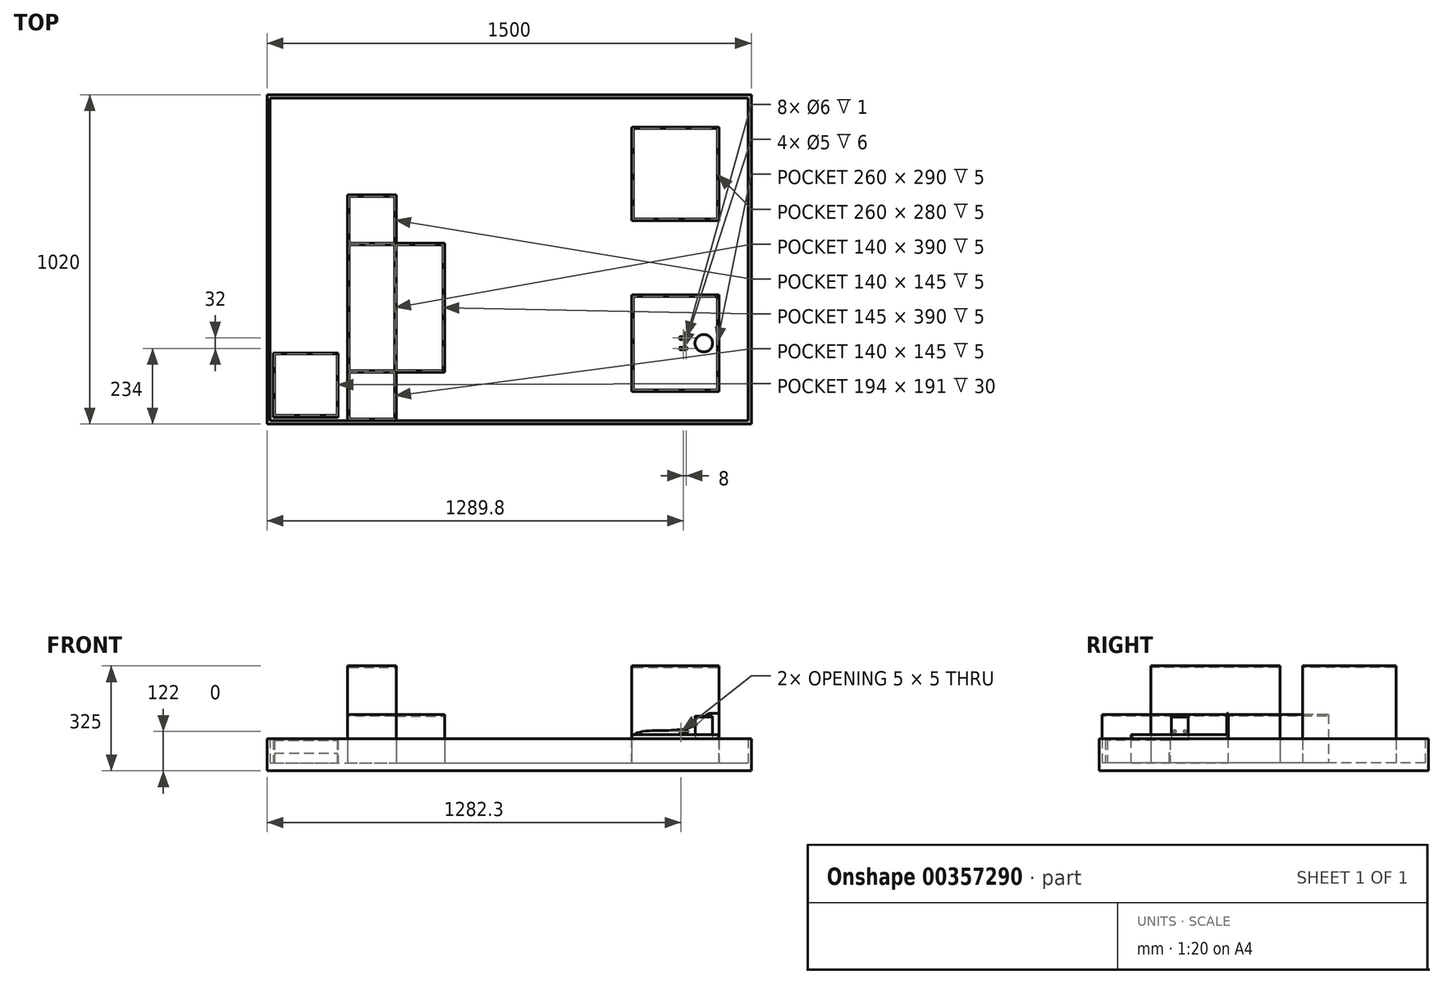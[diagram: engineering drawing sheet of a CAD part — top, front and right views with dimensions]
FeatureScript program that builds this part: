
annotation { "Feature Type Name" : "Feature", "Feature Type Description" : "" }
export const myFeature = defineFeature(function(context is Context, id is Id, definition is map)
    precondition{}
    {
        {
            var Q0;
            Q0=qCreatedBy(makeId("Top.planeOp"),FACE);
            var sketch = newSketch(context, id + "F0", { "sketchPlane" : qUnion([Q0])});
            skCircle(sketch, "E0", {"center": v(0, 0) * mm, "radius": 27.2 * mm});
            skSolve(sketch);
        }
        {
            var Q0;
            Q0=qSketchRegion(id+"F0",true);
            extrude(context, id + "F1", {"entities" : qUnion([Q0]), "depth" : 2.83 * mm});
        }
        {
            var Q0;
            Q0=makeQuery(id+"F1.opExtrude","CAP_FACE",FACE,{"disambiguationData":[OSD([sQuery(id+"F0.wireOp",EDGE,"E0")])],"isStart":false});
            var sketch = newSketch(context, id + "F2", { "sketchPlane" : qUnion([Q0])});
            skCircle(sketch, "E1", {"center": v(0, 0) * mm, "radius": 26.4 * mm});
            skSolve(sketch);
        }
        {
            var Q0;
            Q0=qSketchRegion(id+"F2",true);
            extrude(context, id + "F3", {"entities" : qUnion([Q0]), "operationType" : NewBodyOperationType.ADD, "depth" : 67.36 * mm});
        }
        {
            var Q0;
            Q0=makeQuery(id+"F3.opExtrude","CAP_FACE",FACE,{"disambiguationData":[OSD([sQuery(id+"F2.wireOp",EDGE,"E1")])],"isStart":false});
            var sketch = newSketch(context, id + "F4", { "sketchPlane" : qUnion([Q0])});
            skCircle(sketch, "E2", {"center": v(0, 0) * mm, "radius": 27.2 * mm});
            skSolve(sketch);
        }
        {
            var Q0;
            Q0=qSketchRegion(id+"F4",true);
            extrude(context, id + "F5", {"entities" : qUnion([Q0]), "operationType" : NewBodyOperationType.ADD, "depth" : 2.83 * mm});
        }
        {
            var Q0;
            Q0=makeQuery(id+"F5.opExtrude","CAP_FACE",FACE,{"disambiguationData":[OSD([sQuery(id+"F4.wireOp",EDGE,"E2")])],"isStart":false});
            var sketch = newSketch(context, id + "F6", { "sketchPlane" : qUnion([Q0])});
            skSolve(sketch);
        }
        {
            var Q0;
            Q0=qCreatedBy(makeId("Top.planeOp"),FACE);
            cPlane(context, id + "F7", {"entities" : qUnion([Q0]), "cplaneType" : CPlaneType.OFFSET, "offset" : 25 * mm, "width" : 150 * mm, "height" : 150 * mm});
        }
        {
            var Q0;
            Q0=makeQuery(id+"F6.imprint","IMPRINT",FACE,{"disambiguationData":[TD([[makeQuery(id+"F6.imprint","IMPRINT",EDGE,{"derivedFrom":makeQuery(id+"F5.opExtrude","CAP_EDGE",EDGE,{"disambiguationData":[OSD([sQuery(id+"F4.wireOp",EDGE,"E2")])],"isStart":false})}),1.0]])]});
            var sketch = newSketch(context, id + "F8", { "sketchPlane" : qUnion([Q0])});
            skSolve(sketch);
        }
        {
            var Q0;
            Q0=qCreatedBy(makeId("Top.planeOp"),FACE);
            var sketch = newSketch(context, id + "F9", { "sketchPlane" : qUnion([Q0])});
            skLineSegment(sketch, "E3.bottom", {"start": v(-222.8, -150) * mm, "end": v(47.2, -150) * mm});
            skLineSegment(sketch, "E3.top", {"start": v(-222.8, 150) * mm, "end": v(47.2, 150) * mm});
            skLineSegment(sketch, "E3.left", {"start": v(-222.8, -150) * mm, "end": v(-222.8, 150) * mm});
            skLineSegment(sketch, "E3.right", {"start": v(47.2, -150) * mm, "end": v(47.2, 150) * mm});
            skSolve(sketch);
        }
        {
            var Q0;
            Q0=qSketchRegion(id+"F9",true);
            extrude(context, id + "F10", {"entities" : qUnion([Q0]), "oppositeDirection" : true, "depth" : 72 * mm});
        }
        {
            var Q0;
            Q0=makeQuery(id+"F10.opExtrude","CAP_FACE",FACE,{"disambiguationData":[OSD([sQuery(id+"F9.wireOp",EDGE,"E3.bottom"),sQuery(id+"F9.wireOp",EDGE,"E3.top"),sQuery(id+"F9.wireOp",EDGE,"E3.left"),sQuery(id+"F9.wireOp",EDGE,"E3.right")])],"isStart":true});
            var sketch = newSketch(context, id + "F11", { "sketchPlane" : qUnion([Q0])});
            skLineSegment(sketch, "E4.bottom", {"start": v(-222.8, -150) * mm, "end": v(47.2, -150) * mm});
            skLineSegment(sketch, "E4.top", {"start": v(-222.8, -145) * mm, "end": v(42.2, -145) * mm});
            skLineSegment(sketch, "E4.left", {"start": v(-222.8, -150) * mm, "end": v(-222.8, -145) * mm});
            skLineSegment(sketch, "E5.bottom", {"start": v(47.2, 150) * mm, "end": v(42.2, 150) * mm});
            skLineSegment(sketch, "E5.left", {"start": v(47.2, 150) * mm, "end": v(47.2, -150) * mm});
            skLineSegment(sketch, "E5.right", {"start": v(42.2, 150) * mm, "end": v(42.2, -145) * mm});
            skSolve(sketch);
        }
        {
            var Q0;
            Q0=qSketchRegion(id+"F11",true);
            extrude(context, id + "F12", {"entities" : qUnion([Q0]), "operationType" : NewBodyOperationType.ADD, "depth" : 15 * mm});
        }
        {
            var Q0;
            Q0=makeQuery(id+"F12.boolean.opBoolean","MERGE",FACE,{"derivedFrom":[makeQuery(id+"F10.opExtrude","SWEPT_FACE",FACE,{"disambiguationData":[OSD([sQuery(id+"F9.wireOp",EDGE,"E3.top")])]}),makeQuery(id+"F12.opExtrude","SWEPT_FACE",FACE,{"disambiguationData":[OSD([sQuery(id+"F11.wireOp",EDGE,"E5.bottom")])]})]});
            var sketch = newSketch(context, id + "F13", { "sketchPlane" : qUnion([Q0])});
            skLineSegment(sketch, "E6", {"start": v(-47.2, 81.36) * mm, "end": v(-21.31, 81.36) * mm});
            skFitSpline(sketch, "E7", {"points": [v(-21.31, 81.36) * mm, v(15.24, 52.01) * mm, v(114.14, 28.17) * mm, v(222.8, 0) * mm], "startDerivative": vector(181.02, 0.3) * mm, "endDerivative": vector(-1.73, -239.85) * mm});
            skLineSegment(sketch, "E8", {"start": v(-47.2, 81.36) * mm, "end": v(-47.2, -72) * mm});
            skLineSegment(sketch, "E9", {"start": v(-47.2, -72) * mm, "end": v(222.8, -72) * mm});
            skLineSegment(sketch, "E10", {"start": v(222.8, -72) * mm, "end": v(222.8, 0) * mm});
            skSolve(sketch);
        }
        {
            var Q0;
            Q0=qSketchRegion(id+"F13",true);
            extrude(context, id + "F14", {"entities" : qUnion([Q0]), "operationType" : NewBodyOperationType.ADD, "oppositeDirection" : true, "depth" : 5 * mm});
        }
        {
            var Q0;
            Q0=makeQuery(id+"F10.opExtrude","CAP_FACE",FACE,{"disambiguationData":[OSD([sQuery(id+"F9.wireOp",EDGE,"E3.bottom"),sQuery(id+"F9.wireOp",EDGE,"E3.top"),sQuery(id+"F9.wireOp",EDGE,"E3.left"),sQuery(id+"F9.wireOp",EDGE,"E3.right")])],"isStart":true});
            var sketch = newSketch(context, id + "F15", { "sketchPlane" : qUnion([Q0])});
            skLineSegment(sketch, "E11.bottom", {"start": v(-222.8, 145) * mm, "end": v(-217.8, 145) * mm});
            skLineSegment(sketch, "E11.top", {"start": v(-222.8, -145) * mm, "end": v(-217.8, -145) * mm});
            skLineSegment(sketch, "E11.left", {"start": v(-222.8, 145) * mm, "end": v(-222.8, -145) * mm});
            skLineSegment(sketch, "E11.right", {"start": v(-217.8, 145) * mm, "end": v(-217.8, -145) * mm});
            skSolve(sketch);
        }
        {
            var Q0;
            Q0=qSketchRegion(id+"F15",true);
            extrude(context, id + "F16", {"entities" : qUnion([Q0]), "operationType" : NewBodyOperationType.ADD, "depth" : 5 * mm});
        }
        {
            var Q0;
            Q0=makeQuery(id+"F10.opExtrude","CAP_FACE",FACE,{"disambiguationData":[OSD([sQuery(id+"F9.wireOp",EDGE,"E3.bottom"),sQuery(id+"F9.wireOp",EDGE,"E3.top"),sQuery(id+"F9.wireOp",EDGE,"E3.left"),sQuery(id+"F9.wireOp",EDGE,"E3.right")])],"isStart":false});
            var sketch = newSketch(context, id + "F17", { "sketchPlane" : qUnion([Q0])});
            skLineSegment(sketch, "E12.bottom", {"start": v(147.2, 250) * mm, "end": v(-1352.8, 250) * mm});
            skLineSegment(sketch, "E12.top", {"start": v(147.2, -770) * mm, "end": v(-1352.8, -770) * mm});
            skLineSegment(sketch, "E12.left", {"start": v(147.2, 250) * mm, "end": v(147.2, -770) * mm});
            skLineSegment(sketch, "E12.right", {"start": v(-1352.8, 250) * mm, "end": v(-1352.8, -770) * mm});
            skSolve(sketch);
        }
        {
            var Q0;
            Q0=qSketchRegion(id+"F17",true);
            extrude(context, id + "F18", {"entities" : qUnion([Q0]), "operationType" : NewBodyOperationType.ADD, "depth" : 25 * mm});
        }
        {
            var Q0;
            Q0=makeQuery(id+"F18.opExtrude","CAP_FACE",FACE,{"disambiguationData":[OSD([sQuery(id+"F17.wireOp",EDGE,"E12.bottom"),sQuery(id+"F17.wireOp",EDGE,"E12.top"),sQuery(id+"F17.wireOp",EDGE,"E12.left"),sQuery(id+"F17.wireOp",EDGE,"E12.right")])],"isStart":true});
            var sketch = newSketch(context, id + "F19", { "sketchPlane" : qUnion([Q0])});
            skLineSegment(sketch, "E13.bottom", {"start": v(-222.8, 670) * mm, "end": v(47.2, 670) * mm});
            skLineSegment(sketch, "E13.top", {"start": v(-222.8, 380) * mm, "end": v(47.2, 380) * mm});
            skLineSegment(sketch, "E13.left", {"start": v(-222.8, 670) * mm, "end": v(-222.8, 380) * mm});
            skLineSegment(sketch, "E13.right", {"start": v(47.2, 670) * mm, "end": v(47.2, 380) * mm});
            skSolve(sketch);
        }
        {
            var Q0;
            Q0=qSketchRegion(id+"F19",true);
            extrude(context, id + "F20", {"entities" : qUnion([Q0]), "operationType" : NewBodyOperationType.ADD, "depth" : 300 * mm});
        }
        {
            var Q0;
            Q0=makeQuery(id+"F20.opExtrude","CAP_FACE",FACE,{"disambiguationData":[OSD([sQuery(id+"F19.wireOp",EDGE,"E13.bottom"),sQuery(id+"F19.wireOp",EDGE,"E13.top"),sQuery(id+"F19.wireOp",EDGE,"E13.left"),sQuery(id+"F19.wireOp",EDGE,"E13.right")])],"isStart":false});
            var sketch = newSketch(context, id + "F21", { "sketchPlane" : qUnion([Q0])});
            skLineSegment(sketch, "E14.bottom", {"start": v(-217.8, 665) * mm, "end": v(42.2, 665) * mm});
            skLineSegment(sketch, "E14.top", {"start": v(-217.8, 385) * mm, "end": v(42.2, 385) * mm});
            skLineSegment(sketch, "E14.left", {"start": v(-217.8, 665) * mm, "end": v(-217.8, 385) * mm});
            skLineSegment(sketch, "E14.right", {"start": v(42.2, 665) * mm, "end": v(42.2, 385) * mm});
            skSolve(sketch);
        }
        {
            var Q0;
            Q0=qSketchRegion(id+"F21",true);
            extrude(context, id + "F22", {"entities" : qUnion([Q0]), "operationType" : NewBodyOperationType.REMOVE, "oppositeDirection" : true, "depth" : 5 * mm});
        }
        {
            var Q0;
            Q0=makeQuery(id+"F18.opExtrude","CAP_FACE",FACE,{"disambiguationData":[OSD([sQuery(id+"F17.wireOp",EDGE,"E12.bottom"),sQuery(id+"F17.wireOp",EDGE,"E12.top"),sQuery(id+"F17.wireOp",EDGE,"E12.left"),sQuery(id+"F17.wireOp",EDGE,"E12.right")])],"isStart":true});
            var sketch = newSketch(context, id + "F23", { "sketchPlane" : qUnion([Q0])});
            skLineSegment(sketch, "E15.bottom", {"start": v(-1352.8, 770) * mm, "end": v(147.2, 770) * mm});
            skLineSegment(sketch, "E15.top", {"start": v(-1352.8, -250) * mm, "end": v(147.2, -250) * mm});
            skLineSegment(sketch, "E15.left", {"start": v(-1352.8, 770) * mm, "end": v(-1352.8, -250) * mm});
            skLineSegment(sketch, "E15.right", {"start": v(147.2, 770) * mm, "end": v(147.2, -250) * mm});
            skLineSegment(sketch, "E16.bottom", {"start": v(-1342.8, 760) * mm, "end": v(137.2, 760) * mm});
            skLineSegment(sketch, "E16.top", {"start": v(-1342.8, -240) * mm, "end": v(137.2, -240) * mm});
            skLineSegment(sketch, "E16.left", {"start": v(-1342.8, 760) * mm, "end": v(-1342.8, -240) * mm});
            skLineSegment(sketch, "E16.right", {"start": v(137.2, 760) * mm, "end": v(137.2, -240) * mm});
            skSolve(sketch);
        }
        {
            var Q0;
            Q0=qSketchRegion(id+"F23",true);
            extrude(context, id + "F24", {"entities" : qUnion([Q0]), "operationType" : NewBodyOperationType.ADD, "depth" : 75 * mm});
        }
        {
            var Q0;
            Q0=makeQuery(id+"F18.opExtrude","CAP_FACE",FACE,{"disambiguationData":[OSD([sQuery(id+"F17.wireOp",EDGE,"E12.bottom"),sQuery(id+"F17.wireOp",EDGE,"E12.top"),sQuery(id+"F17.wireOp",EDGE,"E12.left"),sQuery(id+"F17.wireOp",EDGE,"E12.right")])],"isStart":true});
            var sketch = newSketch(context, id + "F25", { "sketchPlane" : qUnion([Q0])});
            skLineSegment(sketch, "E17.bottom", {"start": v(-1102.8, 460) * mm, "end": v(-952.8, 460) * mm});
            skLineSegment(sketch, "E17.top", {"start": v(-1102.8, -240) * mm, "end": v(-952.8, -240) * mm});
            skLineSegment(sketch, "E17.left", {"start": v(-1102.8, 460) * mm, "end": v(-1102.8, -240) * mm});
            skLineSegment(sketch, "E17.right", {"start": v(-952.8, 460) * mm, "end": v(-952.8, 310) * mm});
            skLineSegment(sketch, "E18.bottom", {"start": v(-952.8, 310) * mm, "end": v(-802.8, 310) * mm});
            skLineSegment(sketch, "E18.top", {"start": v(-952.8, -90) * mm, "end": v(-802.8, -90) * mm});
            skLineSegment(sketch, "E18.right", {"start": v(-802.8, 310) * mm, "end": v(-802.8, -90) * mm});
            skLineSegment(sketch, "E19.trimOffspring", {"start": v(-952.8, -90) * mm, "end": v(-952.8, -240) * mm});
            skSolve(sketch);
        }
        {
            var Q0;
            Q0=qSketchRegion(id+"F25",true);
            extrude(context, id + "F26", {"entities" : qUnion([Q0]), "operationType" : NewBodyOperationType.ADD, "depth" : 150 * mm});
        }
        {
            var Q0;
            Q0=makeQuery(id+"F26.opExtrude","CAP_FACE",FACE,{"disambiguationData":[OSD([sQuery(id+"F25.wireOp",EDGE,"E17.bottom"),sQuery(id+"F25.wireOp",EDGE,"E17.top"),sQuery(id+"F25.wireOp",EDGE,"E17.left"),sQuery(id+"F25.wireOp",EDGE,"E17.right"),sQuery(id+"F25.wireOp",EDGE,"E18.bottom"),sQuery(id+"F25.wireOp",EDGE,"E18.top"),sQuery(id+"F25.wireOp",EDGE,"E18.right"),sQuery(id+"F25.wireOp",EDGE,"E19.trimOffspring")])],"isStart":false});
            var sketch = newSketch(context, id + "F27", { "sketchPlane" : qUnion([Q0])});
            skLineSegment(sketch, "E20.bottom", {"start": v(-952.8, 310) * mm, "end": v(-1102.8, 310) * mm});
            skLineSegment(sketch, "E20.top", {"start": v(-952.8, -90) * mm, "end": v(-1102.8, -90) * mm});
            skLineSegment(sketch, "E20.left", {"start": v(-952.8, 310) * mm, "end": v(-952.8, -90) * mm});
            skLineSegment(sketch, "E20.right", {"start": v(-1102.8, 310) * mm, "end": v(-1102.8, -90) * mm});
            skSolve(sketch);
        }
        {
            var Q0;
            Q0=qSketchRegion(id+"F27",true);
            extrude(context, id + "F28", {"entities" : qUnion([Q0]), "operationType" : NewBodyOperationType.ADD, "depth" : 150 * mm});
        }
        {
            var Q0;
            Q0=makeQuery(id+"F28.opExtrude","CAP_FACE",FACE,{"disambiguationData":[OSD([sQuery(id+"F27.wireOp",EDGE,"E20.bottom"),sQuery(id+"F27.wireOp",EDGE,"E20.top"),sQuery(id+"F27.wireOp",EDGE,"E20.left"),sQuery(id+"F27.wireOp",EDGE,"E20.right")])],"isStart":false});
            var sketch = newSketch(context, id + "F29", { "sketchPlane" : qUnion([Q0])});
            skLineSegment(sketch, "E21.bottom", {"start": v(-1097.8, 305) * mm, "end": v(-957.8, 305) * mm});
            skLineSegment(sketch, "E21.top", {"start": v(-1097.8, -85) * mm, "end": v(-957.8, -85) * mm});
            skLineSegment(sketch, "E21.left", {"start": v(-1097.8, 305) * mm, "end": v(-1097.8, -85) * mm});
            skLineSegment(sketch, "E21.right", {"start": v(-957.8, 305) * mm, "end": v(-957.8, -85) * mm});
            skSolve(sketch);
        }
        {
            var Q0;
            Q0=qSketchRegion(id+"F29",true);
            extrude(context, id + "F30", {"entities" : qUnion([Q0]), "operationType" : NewBodyOperationType.REMOVE, "oppositeDirection" : true, "depth" : 5 * mm});
        }
        {
            var Q0;
            {var subQ0=sQuery(id+"F25.wireOp",EDGE,"E17.left");var subQ1=sQuery(id+"F25.wireOp",EDGE,"E18.bottom");var subQ2=sQuery(id+"F25.wireOp",EDGE,"E17.right");var subQ3=sQuery(id+"F25.wireOp",EDGE,"E17.bottom");var subQ4=makeQuery(id+"F26.opExtrude","CAP_FACE",FACE,{"disambiguationData":[OSD([subQ3,sQuery(id+"F25.wireOp",EDGE,"E17.top"),subQ0,subQ2,subQ1,sQuery(id+"F25.wireOp",EDGE,"E18.top"),sQuery(id+"F25.wireOp",EDGE,"E18.right"),sQuery(id+"F25.wireOp",EDGE,"E19.trimOffspring")])],"isStart":false});Q0=makeQuery(id+"F28.boolean.opBoolean","SPLIT",FACE,{"disambiguationData":[TD([makeQuery(id+"F26.opExtrude","SWEPT_FACE",FACE,{"disambiguationData":[OSD([subQ3])]})])],"derivedFrom":subQ4});}
            var sketch = newSketch(context, id + "F31", { "sketchPlane" : qUnion([Q0])});
            skLineSegment(sketch, "E22.bottom", {"start": v(-1097.8, 455) * mm, "end": v(-957.8, 455) * mm});
            skLineSegment(sketch, "E22.top", {"start": v(-1097.8, 310) * mm, "end": v(-957.8, 310) * mm});
            skLineSegment(sketch, "E22.left", {"start": v(-1097.8, 455) * mm, "end": v(-1097.8, 310) * mm});
            skLineSegment(sketch, "E22.right", {"start": v(-957.8, 455) * mm, "end": v(-957.8, 310) * mm});
            skLineSegment(sketch, "E23.bottom", {"start": v(-952.8, 305) * mm, "end": v(-807.8, 305) * mm});
            skLineSegment(sketch, "E23.top", {"start": v(-952.8, -85) * mm, "end": v(-807.8, -85) * mm});
            skLineSegment(sketch, "E23.left", {"start": v(-952.8, 305) * mm, "end": v(-952.8, -85) * mm});
            skLineSegment(sketch, "E23.right", {"start": v(-807.8, 305) * mm, "end": v(-807.8, -85) * mm});
            skLineSegment(sketch, "E24.bottom", {"start": v(-1097.8, -90) * mm, "end": v(-957.8, -90) * mm});
            skLineSegment(sketch, "E24.top", {"start": v(-1097.8, -235) * mm, "end": v(-957.8, -235) * mm});
            skLineSegment(sketch, "E24.left", {"start": v(-1097.8, -90) * mm, "end": v(-1097.8, -235) * mm});
            skLineSegment(sketch, "E24.right", {"start": v(-957.8, -90) * mm, "end": v(-957.8, -235) * mm});
            skSolve(sketch);
        }
        {
            var Q0;
            Q0=qSketchRegion(id+"F31",true);
            extrude(context, id + "F32", {"entities" : qUnion([Q0]), "operationType" : NewBodyOperationType.REMOVE, "oppositeDirection" : true, "depth" : 5 * mm});
        }
        {
            var Q0;
            Q0=qCreatedBy(id+"F7.planeOp",FACE);
            var sketch = newSketch(context, id + "F33", { "sketchPlane" : qUnion([Q0])});
            skLineSegment(sketch, "E25", {"start": v(0, 0) * mm, "end": v(-90, 0) * mm, "construction": true});
            skLineSegment(sketch, "E26.bottom", {"start": v(-74.5, -12) * mm, "end": v(-55, -12) * mm});
            skLineSegment(sketch, "E26.top", {"start": v(-74.5, -20) * mm, "end": v(-55, -20) * mm});
            skLineSegment(sketch, "E26.left", {"start": v(-74.5, -12) * mm, "end": v(-74.5, -13) * mm});
            skPoint(sketch, "E27.visualSharp", {"position": v(-51, -12) * mm});
            skPoint(sketch, "E28.visualSharp", {"position": v(-51, -20) * mm});
            skCircle(sketch, "E29", {"center": v(-55, -16) * mm, "radius": 3 * mm});
            skLineSegment(sketch, "E30", {"start": v(-59, -3.98) * mm, "end": v(-59, -18.08) * mm, "construction": true});
            skCircle(sketch, "E31.MirrorC", {"center": v(-63, -16) * mm, "radius": 3 * mm});
            skLineSegment(sketch, "E32.bottom", {"start": v(-74.5, -13) * mm, "end": v(-65.65, -13) * mm});
            skLineSegment(sketch, "E32.top", {"start": v(-74.5, -19) * mm, "end": v(-65.65, -19) * mm});
            skArc(sketch, "E33", {"start": v(-65.65, -13) * mm, "mid": v(-67, -16) * mm, "end": v(-65.65, -19) * mm});
            skLineSegment(sketch, "E34.trimOffspring", {"start": v(-74.5, -19) * mm, "end": v(-74.5, -20) * mm});
            skArc(sketch, "E35.trimOffspring", {"start": v(-55, -20) * mm, "mid": v(-51, -16) * mm, "end": v(-55, -12) * mm});
            skLineSegment(sketch, "E36.MirrorCS", {"start": v(-74.5, 12) * mm, "end": v(-74.5, 13) * mm});
            skLineSegment(sketch, "E37.MirrorCS", {"start": v(-74.5, 19) * mm, "end": v(-74.5, 20) * mm});
            skPoint(sketch, "E38.MirrorP", {"position": v(-51, 12) * mm});
            skLineSegment(sketch, "E39.MirrorCS", {"start": v(-74.5, 12) * mm, "end": v(-55, 12) * mm});
            skPoint(sketch, "E40.MirrorP", {"position": v(-51, 20) * mm});
            skArc(sketch, "E41.MirrorCS", {"start": v(-65.65, 13) * mm, "mid": v(-67, 16) * mm, "end": v(-65.65, 19) * mm});
            skArc(sketch, "E42.MirrorCS", {"start": v(-55, 20) * mm, "mid": v(-51, 16) * mm, "end": v(-55, 12) * mm});
            skLineSegment(sketch, "E43.MirrorCS", {"start": v(-74.5, 20) * mm, "end": v(-55, 20) * mm});
            skCircle(sketch, "E44.MirrorC", {"center": v(-55, 16) * mm, "radius": 3 * mm});
            skCircle(sketch, "E45.MirrorC", {"center": v(-63, 16) * mm, "radius": 3 * mm});
            skLineSegment(sketch, "E46.MirrorCS", {"start": v(-74.5, 19) * mm, "end": v(-65.65, 19) * mm});
            skLineSegment(sketch, "E47.MirrorCS", {"start": v(-74.5, 13) * mm, "end": v(-65.65, 13) * mm});
            skSolve(sketch);
        }
        {
            var Q0;
            Q0=qSketchRegion(id+"F33",true);
            var Q1;
            Q1=qSketchRegion(id+"F36",true);
            extrude(context, id + "F34", {"entities" : qUnion([Q0, Q1]), "endBound" : BoundingType.SYMMETRIC, "depth" : 8 * mm});
        }
        {
            var Q0;
            Q0=makeQuery(id+"F34.opExtrude","CAP_EDGE",EDGE,{"disambiguationData":[OSD([sQuery(id+"F33.wireOp",EDGE,"E34.trimOffspring")])],"isStart":false});
            var Q1;
            Q1=makeQuery(id+"F34.opExtrude","CAP_EDGE",EDGE,{"disambiguationData":[OSD([sQuery(id+"F33.wireOp",EDGE,"E26.left")])],"isStart":false});
            var Q2;
            Q2=makeQuery(id+"F34.opExtrude","CAP_EDGE",EDGE,{"disambiguationData":[OSD([sQuery(id+"F33.wireOp",EDGE,"E34.trimOffspring")])],"isStart":true});
            var Q3;
            Q3=makeQuery(id+"F34.opExtrude","CAP_EDGE",EDGE,{"disambiguationData":[OSD([sQuery(id+"F33.wireOp",EDGE,"E26.left")])],"isStart":true});
            var Q4;
            Q4=makeQuery(id+"F34.opExtrude","CAP_EDGE",EDGE,{"disambiguationData":[OSD([sQuery(id+"F33.wireOp",EDGE,"E36.MirrorCS")])],"isStart":false});
            var Q5;
            Q5=makeQuery(id+"F34.opExtrude","CAP_EDGE",EDGE,{"disambiguationData":[OSD([sQuery(id+"F33.wireOp",EDGE,"E37.MirrorCS")])],"isStart":false});
            var Q6;
            Q6=makeQuery(id+"F34.opExtrude","CAP_EDGE",EDGE,{"disambiguationData":[OSD([sQuery(id+"F33.wireOp",EDGE,"E37.MirrorCS")])],"isStart":true});
            var Q7;
            Q7=makeQuery(id+"F34.opExtrude","CAP_EDGE",EDGE,{"disambiguationData":[OSD([sQuery(id+"F33.wireOp",EDGE,"E36.MirrorCS")])],"isStart":true});
            fillet(context, id + "F35", {"entities" : qUnion([Q0, Q1, Q2, Q3, Q4, Q5, Q6, Q7]), "radius" : 4 * mm, "tangentPropagation" : true, "allowEdgeOverflow" : false});
        }
        {
            var Q0;
            Q0=makeQuery(id+"F34.opExtrude","SWEPT_FACE",FACE,{"disambiguationData":[OSD([sQuery(id+"F33.wireOp",EDGE,"E26.top")])]});
            var sketch = newSketch(context, id + "F36", { "sketchPlane" : qUnion([Q0])});
            skCircle(sketch, "E48", {"center": v(-70.5, 25) * mm, "radius": 3 * mm});
            skSolve(sketch);
        }
        {
            var Q0;
            Q0=qSketchRegion(id+"F36",true);
            var Q1;
            Q1=makeQuery(id+"F34.opExtrude","SWEPT_FACE",FACE,{"disambiguationData":[OSD([sQuery(id+"F33.wireOp",EDGE,"E26.bottom")])]});
            extrude(context, id + "F37", {"entities" : qUnion([Q0]), "operationType" : NewBodyOperationType.ADD, "endBound" : BoundingType.UP_TO_SURFACE, "oppositeDirection" : true, "endBoundEntityFace" : qUnion([Q1]), "depth" : 25 * mm});
        }
        {
            var Q0;
            Q0=makeQuery(id+"F34.opExtrude","SWEPT_FACE",FACE,{"disambiguationData":[OSD([sQuery(id+"F33.wireOp",EDGE,"E43.MirrorCS")])]});
            var sketch = newSketch(context, id + "F38", { "sketchPlane" : qUnion([Q0])});
            skCircle(sketch, "E49", {"center": v(70.5, 25) * mm, "radius": 3 * mm});
            skSolve(sketch);
        }
        {
            var Q0;
            Q0=qSketchRegion(id+"F38",true);
            var Q1;
            Q1=makeQuery(id+"F34.opExtrude","SWEPT_FACE",FACE,{"disambiguationData":[OSD([sQuery(id+"F33.wireOp",EDGE,"E39.MirrorCS")])]});
            extrude(context, id + "F39", {"entities" : qUnion([Q0]), "operationType" : NewBodyOperationType.ADD, "endBound" : BoundingType.UP_TO_SURFACE, "oppositeDirection" : true, "endBoundEntityFace" : qUnion([Q1]), "depth" : 25 * mm});
        }
        {
            var Q0;
            Q0=qCreatedBy(id+"F7.planeOp",FACE);
            var sketch = newSketch(context, id + "F40", { "sketchPlane" : qUnion([Q0])});
            skCircle(sketch, "E50", {"center": v(-55, 16) * mm, "radius": 3 * mm});
            skCircle(sketch, "E51", {"center": v(-63, 16) * mm, "radius": 2.5 * mm});
            skCircle(sketch, "E52", {"center": v(-63, 16) * mm, "radius": 3 * mm});
            skCircle(sketch, "E53", {"center": v(-55, 16) * mm, "radius": 2.5 * mm});
            skSolve(sketch);
        }
        {
            var Q0;
            Q0=qSketchRegion(id+"F40",true);
            extrude(context, id + "F41", {"entities" : qUnion([Q0]), "operationType" : NewBodyOperationType.ADD, "endBound" : BoundingType.SYMMETRIC, "depth" : 6 * mm});
        }
        {
            var Q0;
            Q0=qCreatedBy(id+"F7.planeOp",FACE);
            var sketch = newSketch(context, id + "F42", { "sketchPlane" : qUnion([Q0])});
            skCircle(sketch, "E54", {"center": v(-63, -16) * mm, "radius": 2.5 * mm});
            skCircle(sketch, "E55", {"center": v(-63, -16) * mm, "radius": 3 * mm});
            skCircle(sketch, "E56", {"center": v(-55, -16) * mm, "radius": 2.5 * mm});
            skCircle(sketch, "E57", {"center": v(-55, -16) * mm, "radius": 3 * mm});
            skSolve(sketch);
        }
        {
            var Q0;
            Q0=qSketchRegion(id+"F42",true);
            extrude(context, id + "F43", {"entities" : qUnion([Q0]), "operationType" : NewBodyOperationType.ADD, "endBound" : BoundingType.SYMMETRIC, "depth" : 6 * mm});
        }
        {
            var Q0;
            Q0=makeQuery(id+"F34.opExtrude","SWEPT_FACE",FACE,{"disambiguationData":[OSD([sQuery(id+"F33.wireOp",EDGE,"E43.MirrorCS")])]});
            var sketch = newSketch(context, id + "F44", { "sketchPlane" : qUnion([Q0])});
            skArc(sketch, "E58", {"start": v(71.5, 27.3) * mm, "mid": v(70.5, 27.5) * mm, "end": v(69.5, 27.3) * mm});
            skLineSegment(sketch, "E59.bottom", {"start": v(68.2, 26) * mm, "end": v(69.5, 26) * mm});
            skLineSegment(sketch, "E59.top", {"start": v(68.2, 24) * mm, "end": v(69.5, 24) * mm});
            skLineSegment(sketch, "E60.left", {"start": v(71.5, 27.3) * mm, "end": v(71.5, 26) * mm});
            skLineSegment(sketch, "E60.right", {"start": v(69.5, 27.3) * mm, "end": v(69.5, 26) * mm});
            skPoint(sketch, "E61.orphan", {"position": v(69.5, 27.8) * mm});
            skPoint(sketch, "E62.orphan", {"position": v(71.5, 27.8) * mm});
            skArc(sketch, "E63.trimOffspring", {"start": v(68.2, 26) * mm, "mid": v(68, 25) * mm, "end": v(68.2, 24) * mm});
            skPoint(sketch, "E59.left.start.orphan", {"position": v(67.32, 26) * mm});
            skPoint(sketch, "E64.orphan", {"position": v(67.32, 24) * mm});
            skArc(sketch, "E65.trimOffspring", {"start": v(69.5, 22.7) * mm, "mid": v(70.5, 22.5) * mm, "end": v(71.5, 22.7) * mm});
            skLineSegment(sketch, "E66.trimOffspring", {"start": v(69.5, 24) * mm, "end": v(69.5, 22.7) * mm});
            skLineSegment(sketch, "E67.trimOffspring", {"start": v(71.5, 26) * mm, "end": v(72.8, 26) * mm});
            skLineSegment(sketch, "E68.trimOffspring", {"start": v(71.5, 24) * mm, "end": v(71.5, 22.7) * mm});
            skLineSegment(sketch, "E69.trimOffspring", {"start": v(71.5, 24) * mm, "end": v(72.8, 24) * mm});
            skPoint(sketch, "E60.top.end.orphan", {"position": v(69.5, 22.2) * mm});
            skPoint(sketch, "E70.orphan", {"position": v(71.5, 22.2) * mm});
            skPoint(sketch, "E59.right.end.orphan", {"position": v(73.68, 24) * mm});
            skPoint(sketch, "E71.orphan", {"position": v(73.68, 26) * mm});
            skArc(sketch, "E72.trimOffspring", {"start": v(72.8, 24) * mm, "mid": v(73, 25) * mm, "end": v(72.8, 26) * mm});
            skSolve(sketch);
        }
        {
            var Q0;
            Q0=qSketchRegion(id+"F44",true);
            extrude(context, id + "F45", {"entities" : qUnion([Q0]), "operationType" : NewBodyOperationType.REMOVE, "endBound" : BoundingType.THROUGH_ALL, "oppositeDirection" : true, "depth" : 25 * mm});
        }
        {
            var Q0;
            Q0=makeQuery(id+"F18.opExtrude","CAP_FACE",FACE,{"disambiguationData":[OSD([sQuery(id+"F17.wireOp",EDGE,"E12.bottom"),sQuery(id+"F17.wireOp",EDGE,"E12.top"),sQuery(id+"F17.wireOp",EDGE,"E12.left"),sQuery(id+"F17.wireOp",EDGE,"E12.right")])],"isStart":true});
            var sketch = newSketch(context, id + "F46", { "sketchPlane" : qUnion([Q0])});
            skLineSegment(sketch, "E73.bottom", {"start": v(-1332.8, -30) * mm, "end": v(-1132.8, -30) * mm});
            skLineSegment(sketch, "E73.top", {"start": v(-1332.8, -230) * mm, "end": v(-1132.8, -230) * mm});
            skLineSegment(sketch, "E73.left", {"start": v(-1332.8, -30) * mm, "end": v(-1332.8, -230) * mm});
            skLineSegment(sketch, "E73.right", {"start": v(-1132.8, -30) * mm, "end": v(-1132.8, -230) * mm});
            skLineSegment(sketch, "E74.bottom", {"start": v(-1329.8, -33) * mm, "end": v(-1135.8, -33) * mm});
            skLineSegment(sketch, "E74.top", {"start": v(-1329.8, -224) * mm, "end": v(-1135.8, -224) * mm});
            skLineSegment(sketch, "E74.left", {"start": v(-1329.8, -33) * mm, "end": v(-1329.8, -224) * mm});
            skLineSegment(sketch, "E74.right", {"start": v(-1135.8, -33) * mm, "end": v(-1135.8, -224) * mm});
            skSolve(sketch);
        }
        {
            var Q0;
            Q0=qSketchRegion(id+"F46",true);
            extrude(context, id + "F47", {"entities" : qUnion([Q0]), "operationType" : NewBodyOperationType.ADD, "depth" : 30 * mm});
        }
        {
            var Q0;
            Q0=makeQuery(id+"F47.opExtrude","CAP_FACE",FACE,{"disambiguationData":[OSD([sQuery(id+"F46.wireOp",EDGE,"E73.bottom"),sQuery(id+"F46.wireOp",EDGE,"E73.top"),sQuery(id+"F46.wireOp",EDGE,"E73.left"),sQuery(id+"F46.wireOp",EDGE,"E73.right"),sQuery(id+"F46.wireOp",EDGE,"E74.bottom"),sQuery(id+"F46.wireOp",EDGE,"E74.top"),sQuery(id+"F46.wireOp",EDGE,"E74.left"),sQuery(id+"F46.wireOp",EDGE,"E74.right")])],"isStart":false});
            var sketch = newSketch(context, id + "F48", { "sketchPlane" : qUnion([Q0])});
            skLineSegment(sketch, "E75.bottom", {"start": v(-1332.8, -30) * mm, "end": v(-1329.8, -30) * mm});
            skLineSegment(sketch, "E75.top", {"start": v(-1332.8, -230) * mm, "end": v(-1329.8, -230) * mm});
            skLineSegment(sketch, "E75.left", {"start": v(-1332.8, -30) * mm, "end": v(-1332.8, -230) * mm});
            skLineSegment(sketch, "E75.right", {"start": v(-1329.8, -30) * mm, "end": v(-1329.8, -224) * mm});
            skLineSegment(sketch, "E76.bottom", {"start": v(-1329.8, -230) * mm, "end": v(-1135.8, -230) * mm});
            skLineSegment(sketch, "E76.top", {"start": v(-1329.8, -224) * mm, "end": v(-1135.8, -224) * mm});
            skLineSegment(sketch, "E77.bottom", {"start": v(-1135.8, -230) * mm, "end": v(-1132.8, -230) * mm});
            skLineSegment(sketch, "E77.top", {"start": v(-1135.8, -30) * mm, "end": v(-1132.8, -30) * mm});
            skLineSegment(sketch, "E77.left", {"start": v(-1135.8, -224) * mm, "end": v(-1135.8, -30) * mm});
            skLineSegment(sketch, "E77.right", {"start": v(-1132.8, -230) * mm, "end": v(-1132.8, -30) * mm});
            skLineSegment(sketch, "E78", {"start": v(-29.27, 38.12) * mm, "end": v(-29.27, -38.33) * mm});
            skPoint(sketch, "E79.start.orphan", {"position": v(-26.53, -38.33) * mm});
            skPoint(sketch, "E80.orphan", {"position": v(-9.02, -38.33) * mm});
            skPoint(sketch, "E81.end.orphan", {"position": v(-2.92, -38.33) * mm});
            skPoint(sketch, "E81.start.orphan", {"position": v(-5.97, -38.33) * mm});
            skLineSegment(sketch, "E82", {"start": v(-29.27, -38.33) * mm, "end": v(-26.53, -38.33) * mm});
            skLineSegment(sketch, "E83.trimOffspring", {"start": v(-9.02, -38.33) * mm, "end": v(-2.92, -38.33) * mm});
            skLineSegment(sketch, "E84", {"start": v(-29.27, -38.33) * mm, "end": v(28.37, -38.33) * mm});
            skLineSegment(sketch, "E85", {"start": v(-29.27, 38.12) * mm, "end": v(27.78, 38.12) * mm});
            skSolve(sketch);
        }
        {
            var Q0;
            Q0=qSketchRegion(id+"F48",true);
            extrude(context, id + "F49", {"entities" : qUnion([Q0]), "operationType" : NewBodyOperationType.ADD, "depth" : 40 * mm});
        }
    });
